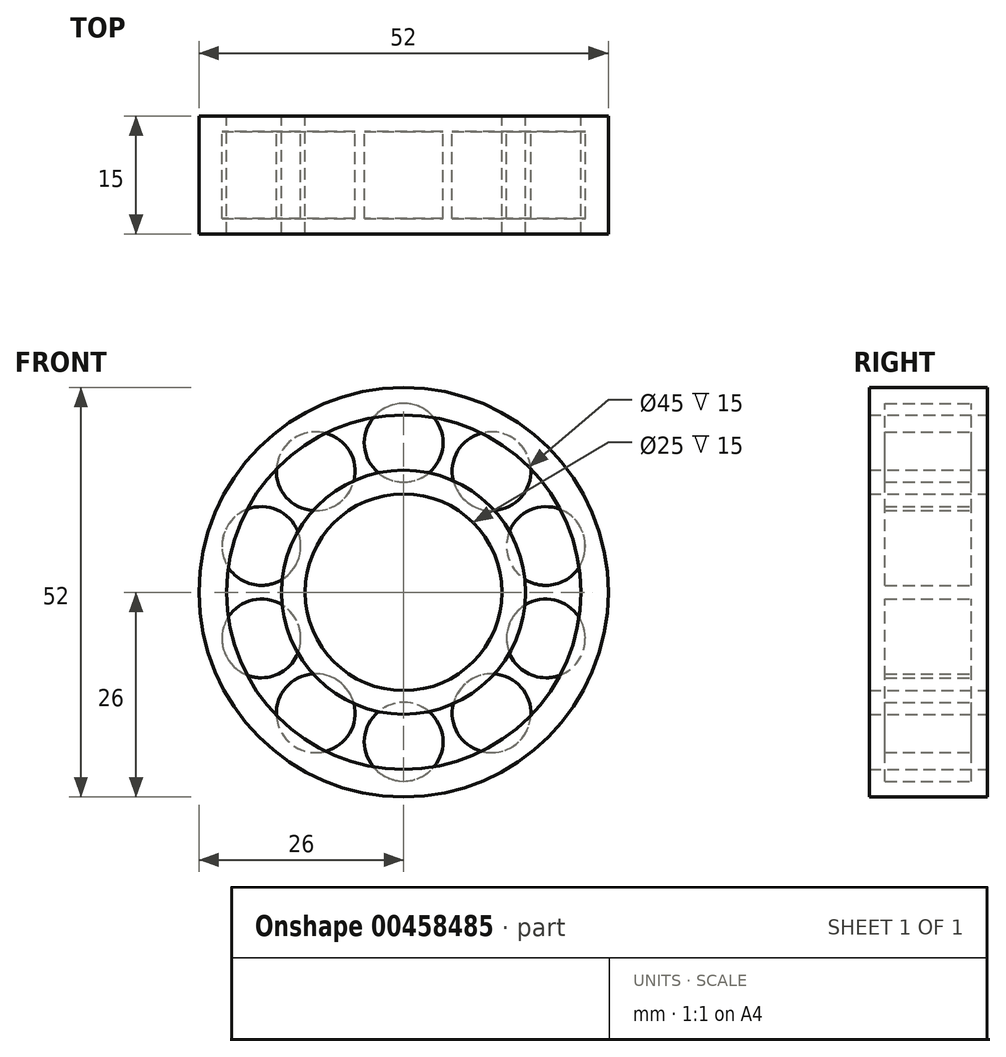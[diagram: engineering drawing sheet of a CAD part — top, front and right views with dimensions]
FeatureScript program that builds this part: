
annotation { "Feature Type Name" : "Feature", "Feature Type Description" : "" }
export const myFeature = defineFeature(function(context is Context, id is Id, definition is map)
    precondition{}
    {
        {
            var Q0;
            Q0=qCreatedBy(makeId("Front.planeOp"),FACE);
            var sketch = newSketch(context, id + "F0", { "sketchPlane" : qUnion([Q0])});
            skCircle(sketch, "E0", {"center": v(0, 0) * mm, "radius": 12.5 * mm});
            skCircle(sketch, "E1", {"center": v(0, 0) * mm, "radius": 15.5 * mm});
            skSolve(sketch);
        }
        {
            var Q0;
            Q0 = qSketchRegion(id + "F0", true);
            extrude(context, id + "F1", {"entities" : qUnion([Q0]), "depth" : 15 * mm});
        }
        {
            var Q0;
            Q0=qCreatedBy(makeId("Front.planeOp"),FACE);
            var sketch = newSketch(context, id + "F2", { "sketchPlane" : qUnion([Q0])});
            skCircle(sketch, "E2", {"center": v(0, 0) * mm, "radius": 22.5 * mm});
            skCircle(sketch, "E3", {"center": v(0, 0) * mm, "radius": 26 * mm});
            skSolve(sketch);
        }
        {
            var Q0;
            Q0 = qSketchRegion(id + "F2", true);
            extrude(context, id + "F3", {"entities" : qUnion([Q0]), "depth" : 15 * mm});
        }
        {
            var Q0;
            Q0=qCreatedBy(makeId("Front.planeOp"),FACE);
            var sketch = newSketch(context, id + "F4", { "sketchPlane" : qUnion([Q0])});
            skCircle(sketch, "E4", {"center": v(-73.83, -37.66) * mm, "radius": 39.5 * mm});
            skSolve(sketch);
        }
        {
            var Q0;
            Q0 = qSketchRegion(id + "F4", true);
            extrude(context, id + "F5", {"entities" : qUnion([Q0]), "depth" : 25 * mm});
        }
        {
            var Q0;
            Q0=makeQuery(id+"F5.opExtrude","SWEPT_BODY",BODY,{"disambiguationData":[OSD([sQuery(id+"F4.wireOp",EDGE,"E4")])]});
            deleteBodies(context, id + "F6", {"entities" : qUnion([Q0])});
        }
        {
            var Q0;
            Q0=qCreatedBy(makeId("Front.planeOp"),FACE);
            cPlane(context, id + "F7", {"entities" : qUnion([Q0]), "cplaneType" : CPlaneType.OFFSET, "offset" : 2 * mm, "width" : 150 * mm, "height" : 150 * mm});
        }
        {
            var Q0;
            Q0=qCreatedBy(id+"F7.planeOp",FACE);
            var sketch = newSketch(context, id + "F8", { "sketchPlane" : qUnion([Q0])});
            skCircle(sketch, "E5", {"center": v(0, 19) * mm, "radius": 5 * mm});
            skCircle(sketch, "E6.1.0", {"center": v(-11.17, 15.37) * mm, "radius": 5 * mm});
            skCircle(sketch, "E6.2.0", {"center": v(-18.07, 5.87) * mm, "radius": 5 * mm});
            skCircle(sketch, "E6.3.0", {"center": v(-18.07, -5.87) * mm, "radius": 5 * mm});
            skCircle(sketch, "E6.4.0", {"center": v(-11.17, -15.37) * mm, "radius": 5 * mm});
            skCircle(sketch, "E6.5.0", {"center": v(0, -19) * mm, "radius": 5 * mm});
            skCircle(sketch, "E6.6.0", {"center": v(11.17, -15.37) * mm, "radius": 5 * mm});
            skCircle(sketch, "E6.7.0", {"center": v(18.07, -5.87) * mm, "radius": 5 * mm});
            skCircle(sketch, "E6.8.0", {"center": v(18.07, 5.87) * mm, "radius": 5 * mm});
            skCircle(sketch, "E6.9.0", {"center": v(11.17, 15.37) * mm, "radius": 5 * mm});
            skPoint(sketch, "E6.center", {"position": v(0, 0) * mm});
            skSolve(sketch);
        }
        {
            var Q0;
            Q0=makeQuery(id+"F8.imprint","IMPRINT",FACE,{"disambiguationData":[TD([[makeQuery(id+"F8.imprint","IMPRINT",EDGE,{"derivedFrom":sQuery(id+"F8.wireOp",EDGE,"E6.1.0")}),1.0]])]});
            var Q1;
            Q1=makeQuery(id+"F8.imprint","IMPRINT",FACE,{"disambiguationData":[TD([[makeQuery(id+"F8.imprint","IMPRINT",EDGE,{"derivedFrom":sQuery(id+"F8.wireOp",EDGE,"E5")}),1.0]])]});
            var Q2;
            Q2=makeQuery(id+"F8.imprint","IMPRINT",FACE,{"disambiguationData":[TD([[makeQuery(id+"F8.imprint","IMPRINT",EDGE,{"derivedFrom":sQuery(id+"F8.wireOp",EDGE,"E6.9.0")}),1.0]])]});
            var Q3;
            Q3=makeQuery(id+"F8.imprint","IMPRINT",FACE,{"disambiguationData":[TD([[makeQuery(id+"F8.imprint","IMPRINT",EDGE,{"derivedFrom":sQuery(id+"F8.wireOp",EDGE,"E6.8.0")}),1.0]])]});
            var Q4;
            Q4=makeQuery(id+"F8.imprint","IMPRINT",FACE,{"disambiguationData":[TD([[makeQuery(id+"F8.imprint","IMPRINT",EDGE,{"derivedFrom":sQuery(id+"F8.wireOp",EDGE,"E6.7.0")}),1.0]])]});
            var Q5;
            Q5=makeQuery(id+"F8.imprint","IMPRINT",FACE,{"disambiguationData":[TD([[makeQuery(id+"F8.imprint","IMPRINT",EDGE,{"derivedFrom":sQuery(id+"F8.wireOp",EDGE,"E6.6.0")}),1.0]])]});
            var Q6;
            Q6=makeQuery(id+"F8.imprint","IMPRINT",FACE,{"disambiguationData":[TD([[makeQuery(id+"F8.imprint","IMPRINT",EDGE,{"derivedFrom":sQuery(id+"F8.wireOp",EDGE,"E6.5.0")}),1.0]])]});
            var Q7;
            Q7=makeQuery(id+"F8.imprint","IMPRINT",FACE,{"disambiguationData":[TD([[makeQuery(id+"F8.imprint","IMPRINT",EDGE,{"derivedFrom":sQuery(id+"F8.wireOp",EDGE,"E6.4.0")}),1.0]])]});
            var Q8;
            Q8=makeQuery(id+"F8.imprint","IMPRINT",FACE,{"disambiguationData":[TD([[makeQuery(id+"F8.imprint","IMPRINT",EDGE,{"derivedFrom":sQuery(id+"F8.wireOp",EDGE,"E6.3.0")}),1.0]])]});
            var Q9;
            Q9=makeQuery(id+"F8.imprint","IMPRINT",FACE,{"disambiguationData":[TD([[makeQuery(id+"F8.imprint","IMPRINT",EDGE,{"derivedFrom":sQuery(id+"F8.wireOp",EDGE,"E6.2.0")}),1.0]])]});
            extrude(context, id + "F9", {"entities" : qUnion([Q0, Q1, Q2, Q3, Q4, Q5, Q6, Q7, Q8, Q9]), "depth" : 11 * mm});
        }
    });
